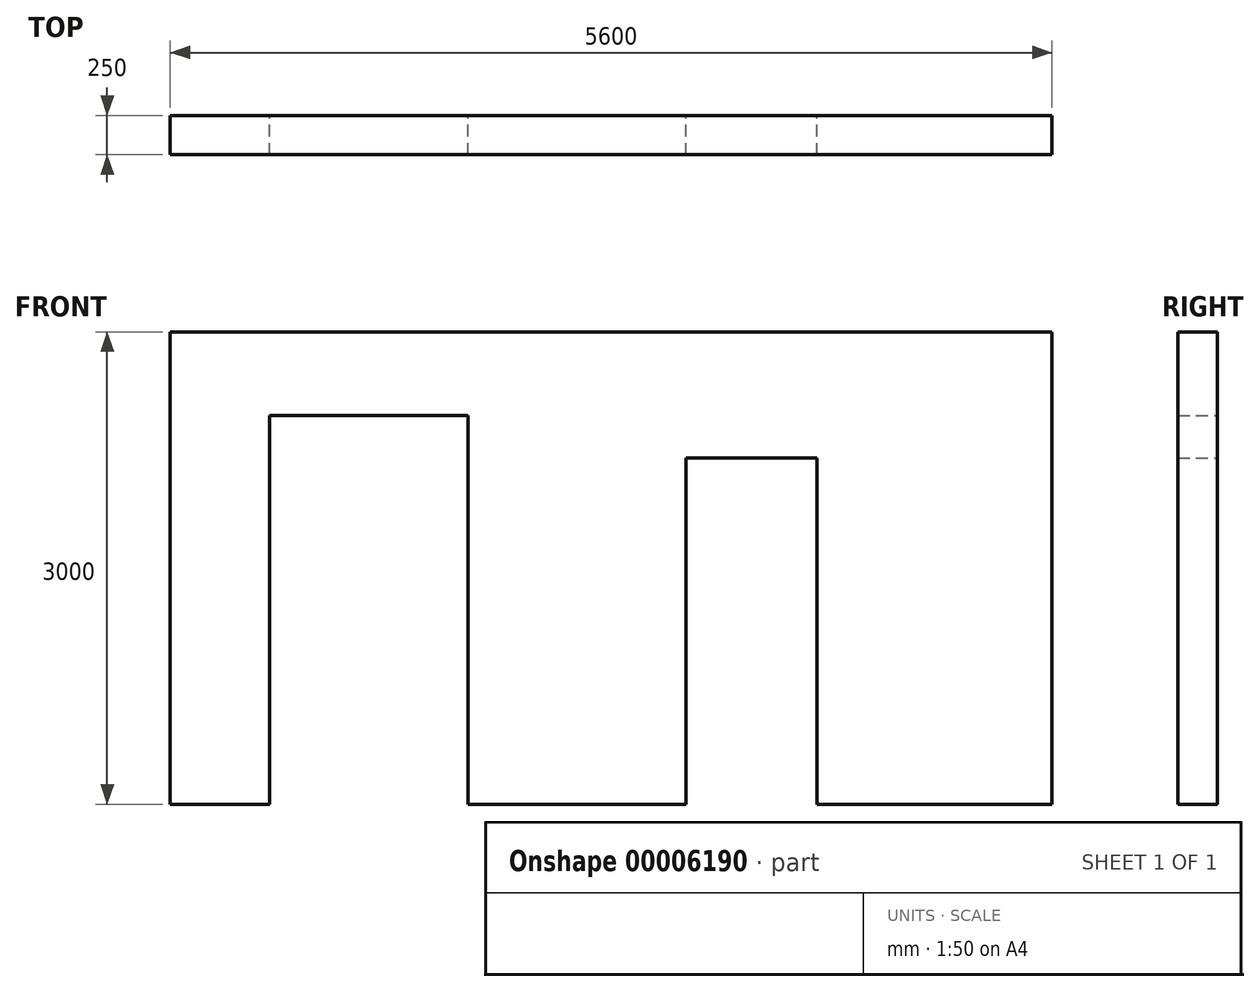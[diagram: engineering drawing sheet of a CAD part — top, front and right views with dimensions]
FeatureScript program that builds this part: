
annotation { "Feature Type Name" : "Feature", "Feature Type Description" : "" }
export const myFeature = defineFeature(function(context is Context, id is Id, definition is map)
    precondition{}
    {
        {
            var Q0;
            Q0=qCreatedBy(makeId("Front.planeOp"),FACE);
            var sketch = newSketch(context, id + "F0", { "sketchPlane" : qUnion([Q0])});
            skLineSegment(sketch, "E0.rect.top", {"start": v(630, 1235) * mm, "end": v(-630, 1235) * mm});
            skLineSegment(sketch, "E0.rect.left", {"start": v(630, -1235) * mm, "end": v(630, 1235) * mm});
            skLineSegment(sketch, "E0.rect.right", {"start": v(-630, -1235) * mm, "end": v(-630, 1235) * mm});
            skPoint(sketch, "E0.rect.middle", {"position": v(0, 0) * mm});
            skLineSegment(sketch, "E1.rect.bottom", {"start": v(4339.7, -1235) * mm, "end": v(630, -1235) * mm});
            skLineSegment(sketch, "E1.rect.top", {"start": v(4339.7, 1765) * mm, "end": v(-1260.3, 1765) * mm});
            skLineSegment(sketch, "E1.rect.left", {"start": v(4339.7, -1235) * mm, "end": v(4339.7, 1765) * mm});
            skLineSegment(sketch, "E1.rect.right", {"start": v(-1260.3, -1235) * mm, "end": v(-1260.3, 1765) * mm});
            skPoint(sketch, "E1.rect.middle", {"position": v(1539.7, 265) * mm});
            skLineSegment(sketch, "E2.trimOffspring", {"start": v(-630, -1235) * mm, "end": v(-1260.3, -1235) * mm});
            skLineSegment(sketch, "E3.rect.bottom", {"start": v(2845.4, -1235) * mm, "end": v(2015.4, -1235) * mm});
            skLineSegment(sketch, "E3.rect.top", {"start": v(2845.4, 965) * mm, "end": v(2015.4, 965) * mm});
            skLineSegment(sketch, "E3.rect.left", {"start": v(2845.4, -1235) * mm, "end": v(2845.4, 965) * mm});
            skLineSegment(sketch, "E3.rect.right", {"start": v(2015.4, -1235) * mm, "end": v(2015.4, 965) * mm});
            skPoint(sketch, "E3.rect.middle", {"position": v(2430.4, -135) * mm});
            skSolve(sketch);
        }
        {
            var Q0;
            Q0=makeQuery(id+"F0.imprint","IMPRINT",FACE,{"disambiguationData":[TD([[makeQuery(id+"F0.imprint","IMPRINT",EDGE,{"derivedFrom":sQuery(id+"F0.wireOp",EDGE,"E0.rect.top")}),-1.0]])]});
            extrude(context, id + "F1", {"entities" : qUnion([Q0]), "depth" : 250 * mm});
        }
    });
